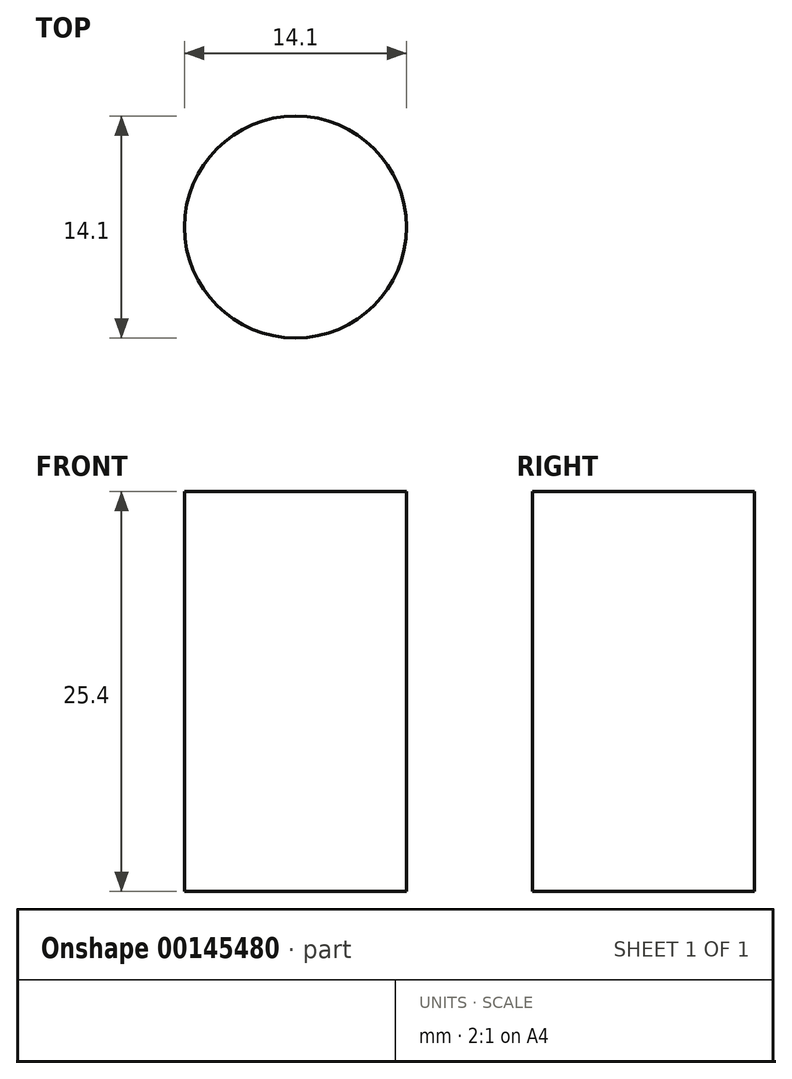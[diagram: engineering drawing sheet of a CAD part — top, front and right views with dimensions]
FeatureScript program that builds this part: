
annotation { "Feature Type Name" : "Feature", "Feature Type Description" : "" }
export const myFeature = defineFeature(function(context is Context, id is Id, definition is map)
    precondition{}
    {
        {
            var Q0;
            Q0=qCreatedBy(makeId("Top.planeOp"),FACE);
            var sketch = newSketch(context, id + "F0", { "sketchPlane" : qUnion([Q0])});
            skCircle(sketch, "E0", {"center": v(0, 0) * mm, "radius": 7.05 * mm});
            skSolve(sketch);
        }
        {
            var Q0;
            Q0=makeQuery(id+"F0.imprint","IMPRINT",FACE,{"disambiguationData":[TD([[makeQuery(id+"F0.imprint","IMPRINT",EDGE,{"derivedFrom":sQuery(id+"F0.wireOp",EDGE,"E0")}),1.0]])]});
            extrude(context, id + "F1", {"entities" : qUnion([Q0]), "depth" : 25.4 * mm});
        }
    });
